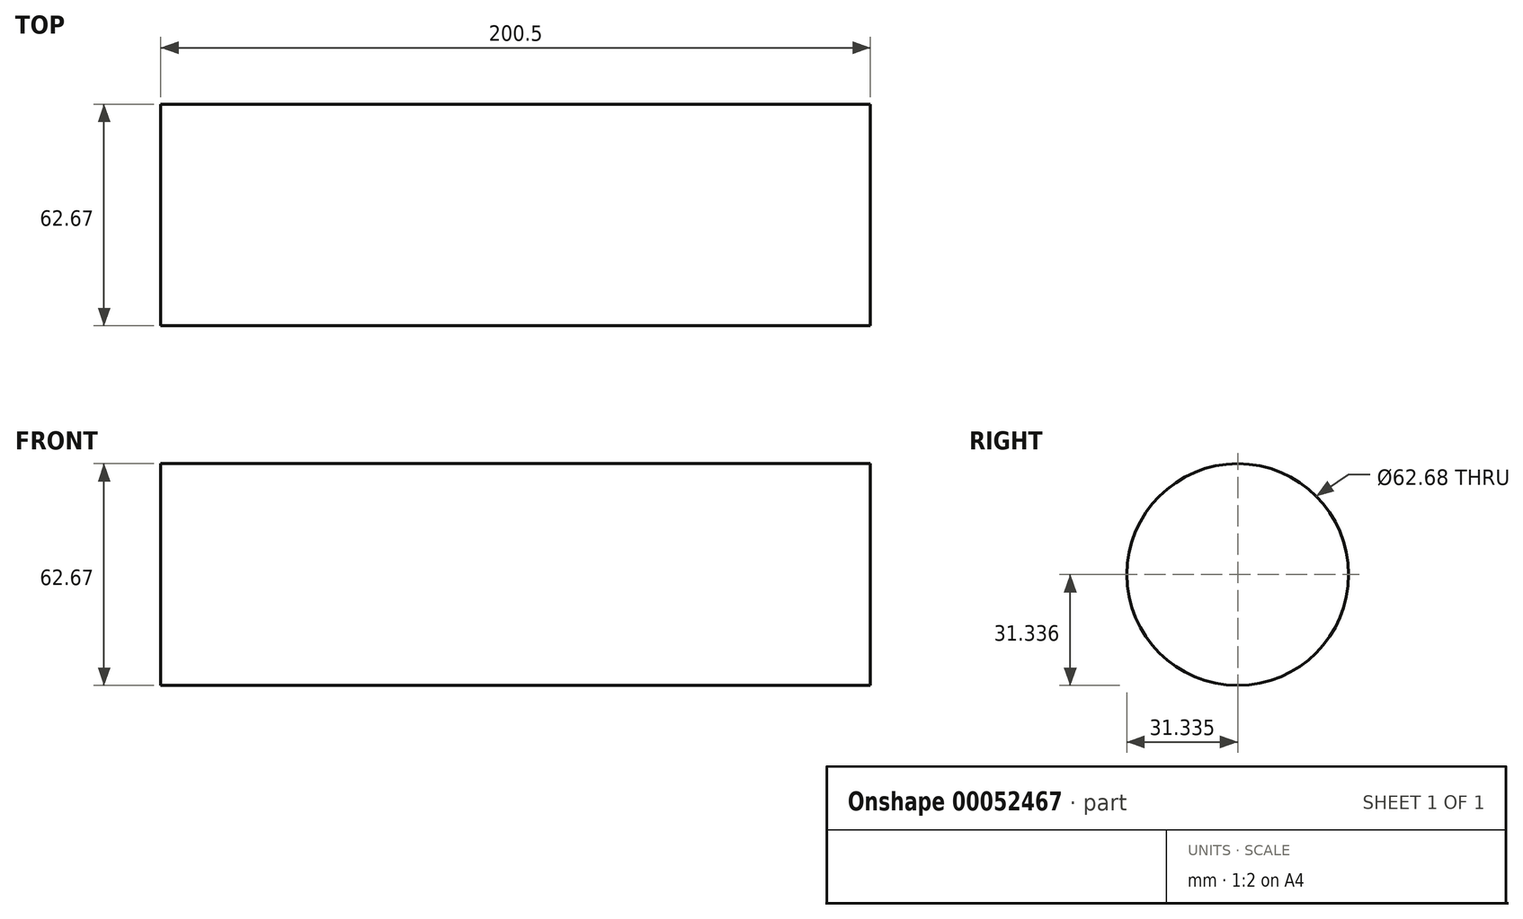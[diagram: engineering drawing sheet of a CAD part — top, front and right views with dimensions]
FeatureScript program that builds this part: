
annotation { "Feature Type Name" : "Feature", "Feature Type Description" : "" }
export const myFeature = defineFeature(function(context is Context, id is Id, definition is map)
    precondition{}
    {
        {
            var Q0;
            Q0=qCreatedBy(makeId("Right.planeOp"),FACE);
            var sketch = newSketch(context, id + "F0", { "sketchPlane" : qUnion([Q0])});
            skCircle(sketch, "E0", {"center": v(-143.68, 6.84) * mm, "radius": 31.34 * mm});
            skCircle(sketch, "E1", {"center": v(-156.21, 35.56) * mm, "radius": 24.7 * mm});
            skSolve(sketch);
        }
        {
            var Q0;
            Q0=sQuery(id+"F0.wireOp",EDGE,"E0");
            extrude(context, id + "F1", {"bodyType" : ToolBodyType.SURFACE, "surfaceEntities" : qUnion([Q0]), "oppositeDirection" : true, "depth" : 99.8 * mm, "hasSecondDirection" : true, "secondDirectionOppositeDirection" : false, "secondDirectionDepth" : 100.7 * mm});
        }
    });
